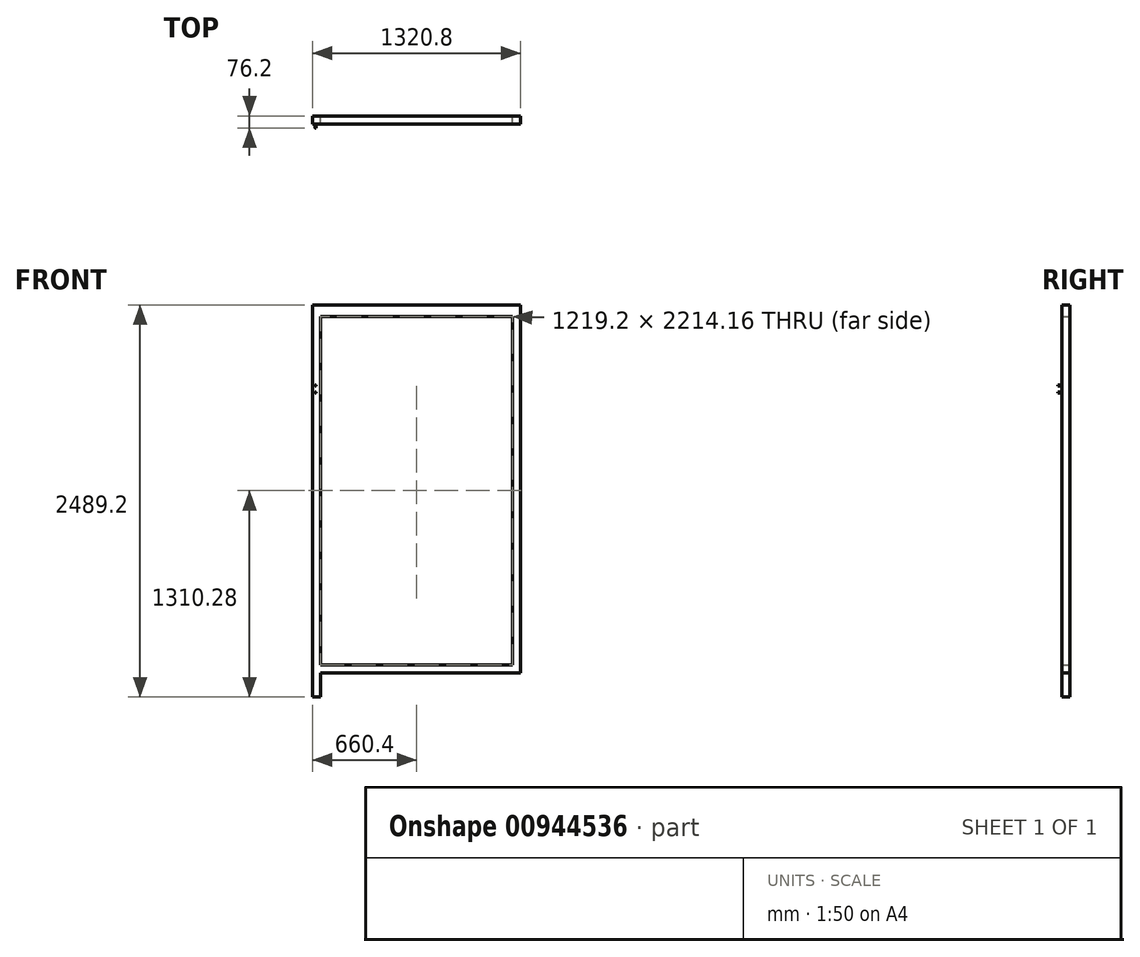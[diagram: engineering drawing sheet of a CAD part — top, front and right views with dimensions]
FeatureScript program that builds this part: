
annotation { "Feature Type Name" : "Feature", "Feature Type Description" : "" }
export const myFeature = defineFeature(function(context is Context, id is Id, definition is map)
    precondition{}
    {
        {
            var Q0;
            Q0=qCreatedBy(makeId("Front.planeOp"),FACE);
            var sketch = newSketch(context, id + "F0", { "sketchPlane" : qUnion([Q0])});
            skLineSegment(sketch, "E0.bottom", {"start": v(-114.47, 2246.75) * mm, "end": v(-63.67, 2246.75) * mm});
            skLineSegment(sketch, "E0.top", {"start": v(-114.47, -90.05) * mm, "end": v(-63.67, -90.05) * mm});
            skLineSegment(sketch, "E0.left", {"start": v(-114.47, 2246.75) * mm, "end": v(-114.47, -90.05) * mm});
            skLineSegment(sketch, "E0.right", {"start": v(-63.67, 2246.75) * mm, "end": v(-63.67, -90.05) * mm});
            skLineSegment(sketch, "E1.bottom", {"start": v(-63.67, -90.05) * mm, "end": v(1155.53, -90.05) * mm});
            skLineSegment(sketch, "E1.top", {"start": v(-63.67, -39.25) * mm, "end": v(1155.53, -39.25) * mm});
            skLineSegment(sketch, "E1.left", {"start": v(-63.67, -90.05) * mm, "end": v(-63.67, -39.25) * mm});
            skLineSegment(sketch, "E1.right", {"start": v(1155.53, -90.05) * mm, "end": v(1155.53, -39.25) * mm});
            skLineSegment(sketch, "E2.bottom", {"start": v(1155.53, -90.05) * mm, "end": v(1206.33, -90.05) * mm});
            skLineSegment(sketch, "E2.top", {"start": v(1155.53, 2246.75) * mm, "end": v(1206.33, 2246.75) * mm});
            skLineSegment(sketch, "E2.left", {"start": v(1155.53, -90.05) * mm, "end": v(1155.53, 2246.75) * mm});
            skLineSegment(sketch, "E2.right", {"start": v(1206.33, -90.05) * mm, "end": v(1206.33, 2246.75) * mm});
            skLineSegment(sketch, "E3.bottom", {"start": v(-63.67, 2246.75) * mm, "end": v(1155.53, 2246.75) * mm});
            skLineSegment(sketch, "E3.top", {"start": v(-63.67, 2174.91) * mm, "end": v(1155.53, 2174.91) * mm});
            skLineSegment(sketch, "E3.left", {"start": v(-63.67, 2246.75) * mm, "end": v(-63.67, 2174.91) * mm});
            skLineSegment(sketch, "E3.right", {"start": v(1155.53, 2246.75) * mm, "end": v(1155.53, 2174.91) * mm});
            skLineSegment(sketch, "E4.bottom", {"start": v(1206.33, -90.05) * mm, "end": v(1155.53, -90.05) * mm});
            skLineSegment(sketch, "E4.top", {"start": v(1206.33, -242.45) * mm, "end": v(1155.53, -242.45) * mm});
            skLineSegment(sketch, "E4.left", {"start": v(1206.33, -90.05) * mm, "end": v(1206.33, -242.45) * mm});
            skLineSegment(sketch, "E4.right", {"start": v(1155.53, -90.05) * mm, "end": v(1155.53, -242.45) * mm});
            skLineSegment(sketch, "E5.top", {"start": v(-114.47, -242.45) * mm, "end": v(-63.67, -242.45) * mm});
            skLineSegment(sketch, "E5.left", {"start": v(-114.47, -90.05) * mm, "end": v(-114.47, -242.45) * mm});
            skLineSegment(sketch, "E5.right", {"start": v(-63.67, -90.05) * mm, "end": v(-63.67, -242.45) * mm});
            skSolve(sketch);
        }
        {
            var Q0;
            {var subQ3=sQuery(id+"F0.wireOp",EDGE,"E2.bottom");Q0=makeQuery(id+"F0.imprint","IMPRINT",FACE,{"disambiguationData":[TD([[makeQuery(id+"F0.imprint","IMPRINT",EDGE,{"derivedFrom":subQ3}),1.0]])]});}
            var Q1;
            Q1=makeQuery(id+"F0.imprint","IMPRINT",FACE,{"disambiguationData":[TD([[makeQuery(id+"F0.imprint","IMPRINT",EDGE,{"derivedFrom":sQuery(id+"F0.wireOp",EDGE,"E3.bottom")}),-1.0]])]});
            var Q2;
            Q2=makeQuery(id+"F0.imprint","IMPRINT",FACE,{"disambiguationData":[TD([[makeQuery(id+"F0.imprint","IMPRINT",EDGE,{"derivedFrom":sQuery(id+"F0.wireOp",EDGE,"E0.bottom")}),-1.0]])]});
            var Q3;
            {var subQ0=sQuery(id+"F0.wireOp",EDGE,"E1.bottom");Q3=makeQuery(id+"F0.imprint","IMPRINT",FACE,{"disambiguationData":[TD([[makeQuery(id+"F0.imprint","IMPRINT",EDGE,{"derivedFrom":subQ0}),1.0]])]});}
            extrude(context, id + "F1", {"entities" : qUnion([Q0, Q1, Q2, Q3]), "depth" : 50.8 * mm, "offsetDistance" : 25.4 * mm});
        }
        {
            var Q0;
            Q0=makeQuery(id+"F1.opExtrude","CAP_FACE",FACE,{"disambiguationData":[OSD([sQuery(id+"F0.wireOp",EDGE,"E0.bottom"),sQuery(id+"F0.wireOp",EDGE,"E0.top"),sQuery(id+"F0.wireOp",EDGE,"E0.left"),sQuery(id+"F0.wireOp",EDGE,"E0.right"),sQuery(id+"F0.wireOp",EDGE,"E1.bottom"),sQuery(id+"F0.wireOp",EDGE,"E1.top"),sQuery(id+"F0.wireOp",EDGE,"E2.bottom"),sQuery(id+"F0.wireOp",EDGE,"E2.top"),sQuery(id+"F0.wireOp",EDGE,"E2.left"),sQuery(id+"F0.wireOp",EDGE,"E2.right"),sQuery(id+"F0.wireOp",EDGE,"E3.bottom"),sQuery(id+"F0.wireOp",EDGE,"E3.top")])],"isStart":false});
            var sketch = newSketch(context, id + "F2", { "sketchPlane" : qUnion([Q0])});
            skCircle(sketch, "E6", {"center": v(-95.42, 1735.58) * mm, "radius": 3.18 * mm});
            skSolve(sketch);
        }
        {
            var Q0;
            Q0=makeQuery(id+"F2.imprint","IMPRINT",FACE,{"disambiguationData":[TD([[makeQuery(id+"F2.imprint","IMPRINT",EDGE,{"derivedFrom":sQuery(id+"F2.wireOp",EDGE,"E6")}),-1.0]])]});
            var sketch = newSketch(context, id + "F3", { "sketchPlane" : qUnion([Q0])});
            skCircle(sketch, "E7", {"center": v(-95.42, 1691.13) * mm, "radius": 3.18 * mm});
            skSolve(sketch);
        }
        {
            var Q0;
            Q0=makeQuery(id+"F3.imprint","IMPRINT",FACE,{"disambiguationData":[TD([[makeQuery(id+"F3.imprint","IMPRINT",EDGE,{"derivedFrom":sQuery(id+"F3.wireOp",EDGE,"E7")}),1.0]])]});
            var Q1;
            Q1=makeQuery(id+"F2.imprint","IMPRINT",FACE,{"disambiguationData":[TD([[makeQuery(id+"F2.imprint","IMPRINT",EDGE,{"derivedFrom":sQuery(id+"F2.wireOp",EDGE,"E6")}),1.0]])]});
            var Q2;
            Q2=makeQuery(id+"F3.imprint","IMPRINT",FACE,{"disambiguationData":[TD([[makeQuery(id+"F3.imprint","IMPRINT",EDGE,{"derivedFrom":makeQuery(id+"F2.imprint","IMPRINT",EDGE,{"derivedFrom":sQuery(id+"F2.wireOp",EDGE,"E6")})}),1.0]])]});
            extrude(context, id + "F4", {"entities" : qUnion([Q0, Q1, Q2]), "operationType" : NewBodyOperationType.ADD, "depth" : 25.4 * mm, "offsetDistance" : 25.4 * mm});
        }
        {
            var Q0;
            Q0=makeQuery(id+"F0.imprint","IMPRINT",FACE,{"disambiguationData":[TD([[makeQuery(id+"F0.imprint","IMPRINT",EDGE,{"derivedFrom":sQuery(id+"F0.wireOp",EDGE,"E2.top")}),-1.0]])]});
            var Q1;
            Q1=makeQuery(id+"F0.imprint","IMPRINT",FACE,{"disambiguationData":[TD([[makeQuery(id+"F0.imprint","IMPRINT",EDGE,{"derivedFrom":sQuery(id+"F0.wireOp",EDGE,"E4.bottom")}),1.0]])]});
            var Q2;
            Q2=makeQuery(id+"F0.imprint","IMPRINT",FACE,{"disambiguationData":[TD([[makeQuery(id+"F0.imprint","IMPRINT",EDGE,{"derivedFrom":sQuery(id+"F0.wireOp",EDGE,"E0.top")}),-1.0]])]});
            extrude(context, id + "F5", {"entities" : qUnion([Q0, Q1, Q2]), "operationType" : NewBodyOperationType.ADD, "depth" : 50.8 * mm, "offsetDistance" : 25.4 * mm});
        }
    });
